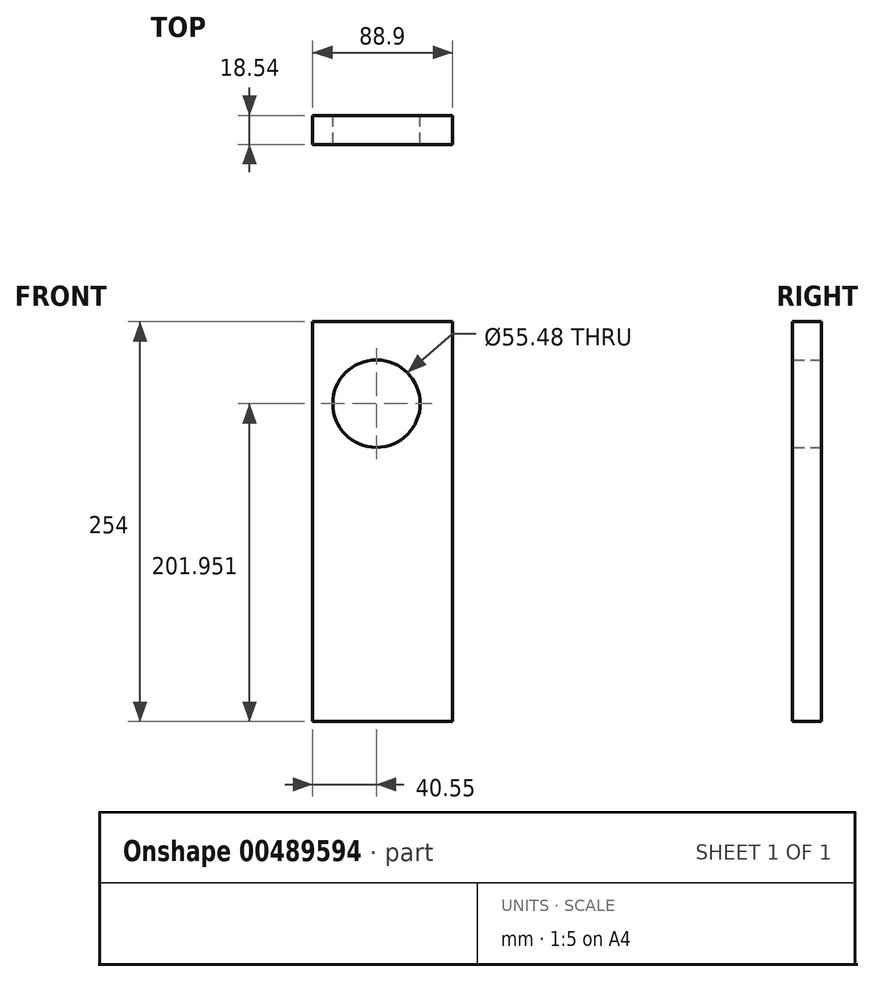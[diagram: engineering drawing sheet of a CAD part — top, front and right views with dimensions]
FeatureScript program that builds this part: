
annotation { "Feature Type Name" : "Feature", "Feature Type Description" : "" }
export const myFeature = defineFeature(function(context is Context, id is Id, definition is map)
    precondition{}
    {
        {
            var Q0;
            Q0=qCreatedBy(makeId("Front.planeOp"),FACE);
            var sketch = newSketch(context, id + "F0", { "sketchPlane" : qUnion([Q0])});
            skLineSegment(sketch, "E0.bottom", {"start": v(-40.55, 173.88) * mm, "end": v(48.35, 173.88) * mm});
            skLineSegment(sketch, "E0.top", {"start": v(-40.55, -80.12) * mm, "end": v(48.35, -80.12) * mm});
            skLineSegment(sketch, "E0.left", {"start": v(-40.55, 173.88) * mm, "end": v(-40.55, -80.12) * mm});
            skLineSegment(sketch, "E0.right", {"start": v(48.35, 173.88) * mm, "end": v(48.35, -80.12) * mm});
            skCircle(sketch, "E1", {"center": v(0, 121.83) * mm, "radius": 27.74 * mm});
            skSolve(sketch);
        }
        {
            var Q0;
            Q0=makeQuery(id+"F0.imprint","IMPRINT",FACE,{"disambiguationData":[TD([[makeQuery(id+"F0.imprint","IMPRINT",EDGE,{"derivedFrom":sQuery(id+"F0.wireOp",EDGE,"E0.bottom")}),-1.0]])]});
            extrude(context, id + "F1", {"entities" : qUnion([Q0]), "depth" : 18.54 * mm, "offsetDistance" : 25.4 * mm});
        }
    });
